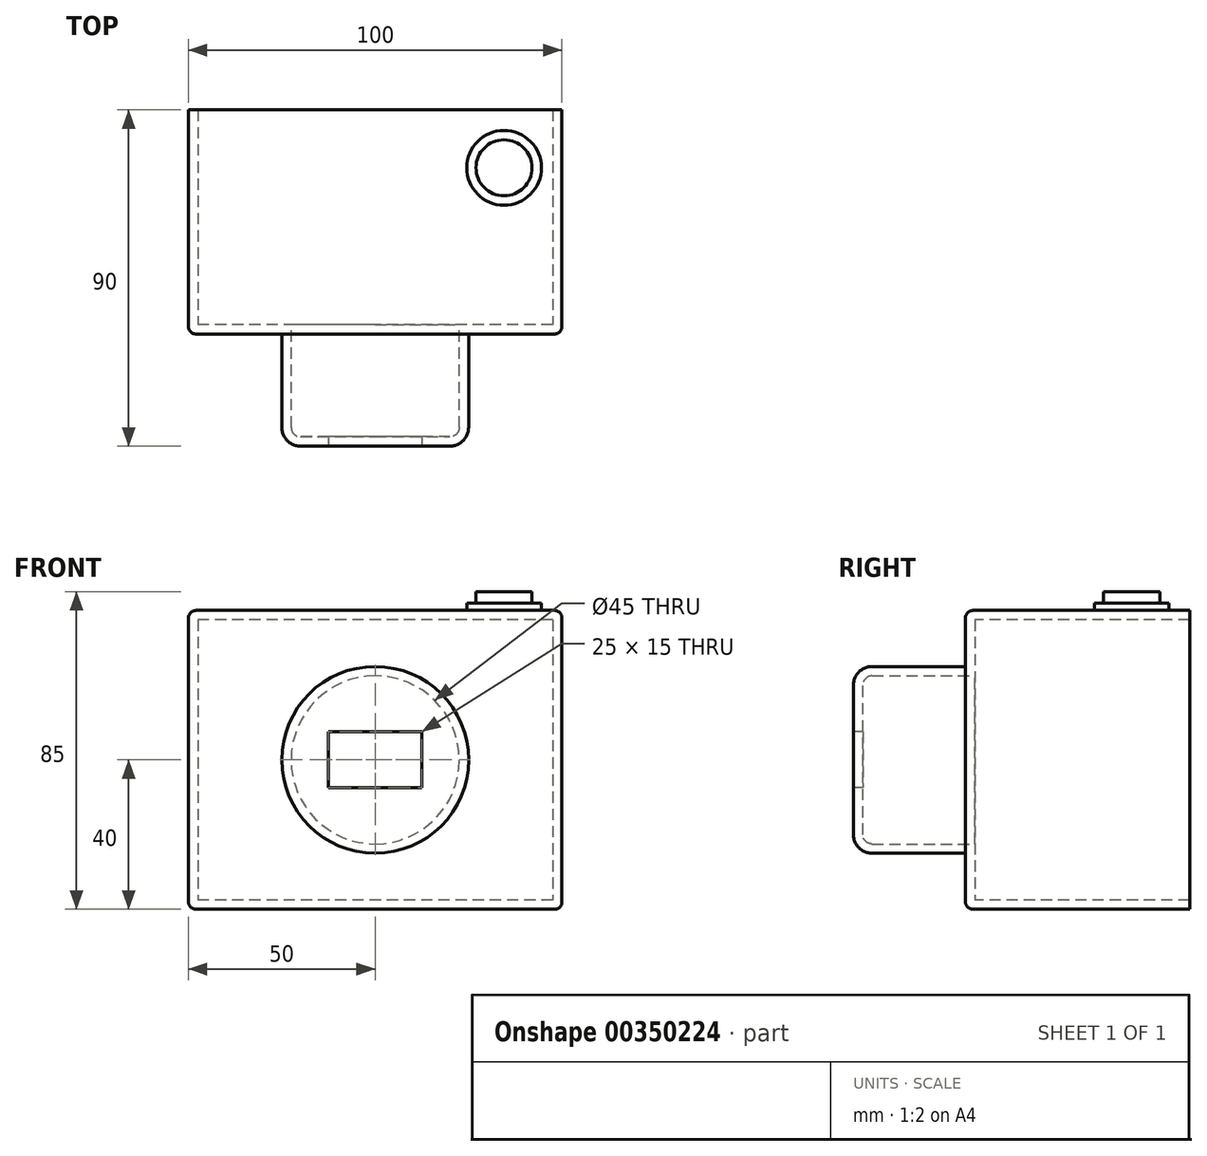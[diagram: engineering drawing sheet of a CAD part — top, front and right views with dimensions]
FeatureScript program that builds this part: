
annotation { "Feature Type Name" : "Feature", "Feature Type Description" : "" }
export const myFeature = defineFeature(function(context is Context, id is Id, definition is map)
    precondition{}
    {
        {
            var Q0;
            Q0=qCreatedBy(makeId("Top.planeOp"),FACE);
            var sketch = newSketch(context, id + "F0", { "sketchPlane" : qUnion([Q0])});
            skLineSegment(sketch, "E0.bottom", {"start": v(50, 30) * mm, "end": v(-50, 30) * mm});
            skLineSegment(sketch, "E0.top", {"start": v(50, -30) * mm, "end": v(-50, -30) * mm});
            skLineSegment(sketch, "E0.left", {"start": v(50, 30) * mm, "end": v(50, -30) * mm});
            skLineSegment(sketch, "E0.right", {"start": v(-50, 30) * mm, "end": v(-50, -30) * mm});
            skPoint(sketch, "E0.middle", {"position": v(0, 0) * mm});
            skSolve(sketch);
        }
        {
            var Q0;
            Q0=makeQuery(id+"F0.imprint","IMPRINT",FACE,{"disambiguationData":[TD([[makeQuery(id+"F0.imprint","IMPRINT",EDGE,{"derivedFrom":sQuery(id+"F0.wireOp",EDGE,"E0.bottom")}),1.0]])]});
            extrude(context, id + "F1", {"entities" : qUnion([Q0]), "endBound" : BoundingType.SYMMETRIC, "depth" : 80 * mm});
        }
        {
            var Q0;
            Q0=makeQuery(id+"F1.opExtrude","SWEPT_FACE",FACE,{"disambiguationData":[OSD([sQuery(id+"F0.wireOp",EDGE,"E0.top")])]});
            var sketch = newSketch(context, id + "F2", { "sketchPlane" : qUnion([Q0])});
            skCircle(sketch, "E1", {"center": v(0, 0) * mm, "radius": 25 * mm});
            skSolve(sketch);
        }
        {
            var Q0;
            Q0=makeQuery(id+"F2.imprint","IMPRINT",FACE,{"disambiguationData":[TD([[makeQuery(id+"F2.imprint","IMPRINT",EDGE,{"derivedFrom":sQuery(id+"F2.wireOp",EDGE,"E1")}),1.0]])]});
            extrude(context, id + "F3", {"entities" : qUnion([Q0]), "operationType" : NewBodyOperationType.ADD, "depth" : 30 * mm});
        }
        {
            var Q0;
            Q0=makeQuery(id+"F3.opExtrude","CAP_FACE",FACE,{"disambiguationData":[OSD([sQuery(id+"F2.wireOp",EDGE,"E1")])],"isStart":false});
            var sketch = newSketch(context, id + "F4", { "sketchPlane" : qUnion([Q0])});
            skLineSegment(sketch, "E2.bottom", {"start": v(12.5, 7.5) * mm, "end": v(-12.5, 7.5) * mm});
            skLineSegment(sketch, "E2.top", {"start": v(12.5, -7.5) * mm, "end": v(-12.5, -7.5) * mm});
            skLineSegment(sketch, "E2.left", {"start": v(12.5, 7.5) * mm, "end": v(12.5, -7.5) * mm});
            skLineSegment(sketch, "E2.right", {"start": v(-12.5, 7.5) * mm, "end": v(-12.5, -7.5) * mm});
            skPoint(sketch, "E2.middle", {"position": v(0, 0) * mm});
            skSolve(sketch);
        }
        {
            var Q0;
            Q0=makeQuery(id+"F3.opExtrude","CAP_EDGE",EDGE,{"disambiguationData":[OSD([sQuery(id+"F2.wireOp",EDGE,"E1")])],"isStart":false});
            var Q1;
            Q1=makeQuery(id+"F3.opExtrude","CAP_EDGE",EDGE,{"disambiguationData":[OSD([sQuery(id+"F2.wireOp",EDGE,"E1")])],"isStart":true});
            fillet(context, id + "F5", {"entities" : qUnion([Q0, Q1]), "radius" : 5 * mm, "tangentPropagation" : true, "allowEdgeOverflow" : false});
        }
        {
            var Q0;
            Q0=makeQuery(id+"F1.opExtrude","SWEPT_FACE",FACE,{"disambiguationData":[OSD([sQuery(id+"F0.wireOp",EDGE,"E0.bottom")])]});
            var Q1;
            Q1=makeQuery(id+"F1.opExtrude","SWEPT_BODY",BODY,{"disambiguationData":[OSD([sQuery(id+"F0.wireOp",EDGE,"E0.bottom"),sQuery(id+"F0.wireOp",EDGE,"E0.top"),sQuery(id+"F0.wireOp",EDGE,"E0.left"),sQuery(id+"F0.wireOp",EDGE,"E0.right")])]});
            shell(context, id + "F6", {"entities" : qUnion([Q0]), "parts" : qUnion([Q1]), "thickness" : 2.5 * mm});
        }
        {
            var Q0;
            Q0=makeQuery(id+"F4.imprint","IMPRINT",FACE,{"disambiguationData":[TD([[makeQuery(id+"F4.imprint","IMPRINT",EDGE,{"derivedFrom":sQuery(id+"F4.wireOp",EDGE,"E2.bottom")}),1.0]])]});
            extrude(context, id + "F7", {"entities" : qUnion([Q0]), "operationType" : NewBodyOperationType.REMOVE, "endBound" : BoundingType.THROUGH_ALL, "oppositeDirection" : true, "depth" : 25 * mm});
        }
        {
            var Q0;
            Q0=makeQuery(id+"F1.opExtrude","CAP_EDGE",EDGE,{"disambiguationData":[OSD([sQuery(id+"F0.wireOp",EDGE,"E0.top")])],"isStart":false});
            var Q1;
            Q1=makeQuery(id+"F1.opExtrude","CAP_EDGE",EDGE,{"disambiguationData":[OSD([sQuery(id+"F0.wireOp",EDGE,"E0.left")])],"isStart":false});
            var Q2;
            Q2=makeQuery(id+"F1.opExtrude","SWEPT_EDGE",EDGE,{"disambiguationData":[OSD([sQuery(id+"F0.wireOp",EDGE,"E0.top"),sQuery(id+"F0.wireOp",EDGE,"E0.left")])]});
            var Q3;
            Q3=makeQuery(id+"F1.opExtrude","SWEPT_EDGE",EDGE,{"disambiguationData":[OSD([sQuery(id+"F0.wireOp",EDGE,"E0.top"),sQuery(id+"F0.wireOp",EDGE,"E0.right")])]});
            var Q4;
            Q4=makeQuery(id+"F1.opExtrude","CAP_EDGE",EDGE,{"disambiguationData":[OSD([sQuery(id+"F0.wireOp",EDGE,"E0.top")])],"isStart":true});
            var Q5;
            Q5=makeQuery(id+"F1.opExtrude","CAP_EDGE",EDGE,{"disambiguationData":[OSD([sQuery(id+"F0.wireOp",EDGE,"E0.right")])],"isStart":true});
            var Q6;
            Q6=makeQuery(id+"F1.opExtrude","CAP_EDGE",EDGE,{"disambiguationData":[OSD([sQuery(id+"F0.wireOp",EDGE,"E0.left")])],"isStart":true});
            var Q7;
            Q7=makeQuery(id+"F1.opExtrude","CAP_EDGE",EDGE,{"disambiguationData":[OSD([sQuery(id+"F0.wireOp",EDGE,"E0.right")])],"isStart":false});
            fillet(context, id + "F8", {"entities" : qUnion([Q0, Q1, Q2, Q3, Q4, Q5, Q6, Q7]), "radius" : 2 * mm, "tangentPropagation" : true, "allowEdgeOverflow" : false});
        }
        {
            var Q0;
            Q0=makeQuery(id+"F1.opExtrude","CAP_FACE",FACE,{"disambiguationData":[OSD([sQuery(id+"F0.wireOp",EDGE,"E0.bottom"),sQuery(id+"F0.wireOp",EDGE,"E0.top"),sQuery(id+"F0.wireOp",EDGE,"E0.left"),sQuery(id+"F0.wireOp",EDGE,"E0.right")])],"isStart":false});
            var sketch = newSketch(context, id + "F9", { "sketchPlane" : qUnion([Q0])});
            skCircle(sketch, "E3", {"center": v(34.5, 14.5) * mm, "radius": 7.5 * mm});
            skSolve(sketch);
        }
        {
            var Q0;
            Q0=makeQuery(id+"F9.imprint","IMPRINT",FACE,{"disambiguationData":[TD([[makeQuery(id+"F9.imprint","IMPRINT",EDGE,{"derivedFrom":sQuery(id+"F9.wireOp",EDGE,"E3")}),1.0]])]});
            extrude(context, id + "F10", {"entities" : qUnion([Q0]), "depth" : 5 * mm});
        }
        {
            var Q0;
            Q0=makeQuery(id+"F1.opExtrude","CAP_FACE",FACE,{"disambiguationData":[OSD([sQuery(id+"F0.wireOp",EDGE,"E0.bottom"),sQuery(id+"F0.wireOp",EDGE,"E0.top"),sQuery(id+"F0.wireOp",EDGE,"E0.left"),sQuery(id+"F0.wireOp",EDGE,"E0.right")])],"isStart":false});
            var sketch = newSketch(context, id + "F11", { "sketchPlane" : qUnion([Q0])});
            skCircle(sketch, "E4", {"center": v(34.5, 14.5) * mm, "radius": 10 * mm});
            skSolve(sketch);
        }
        {
            var Q0;
            Q0=makeQuery(id+"F11.imprint","IMPRINT",FACE,{"disambiguationData":[TD([[makeQuery(id+"F11.imprint","IMPRINT",EDGE,{"derivedFrom":sQuery(id+"F11.wireOp",EDGE,"E4")}),1.0]])]});
            var Q1;
            Q1=sQuery(id+"F11.wireOp",EDGE,"E4");
            extrude(context, id + "F12", {"entities" : qUnion([Q0]), "operationType" : NewBodyOperationType.ADD, "surfaceEntities" : qUnion([Q1]), "depth" : 2 * mm});
        }
    });
